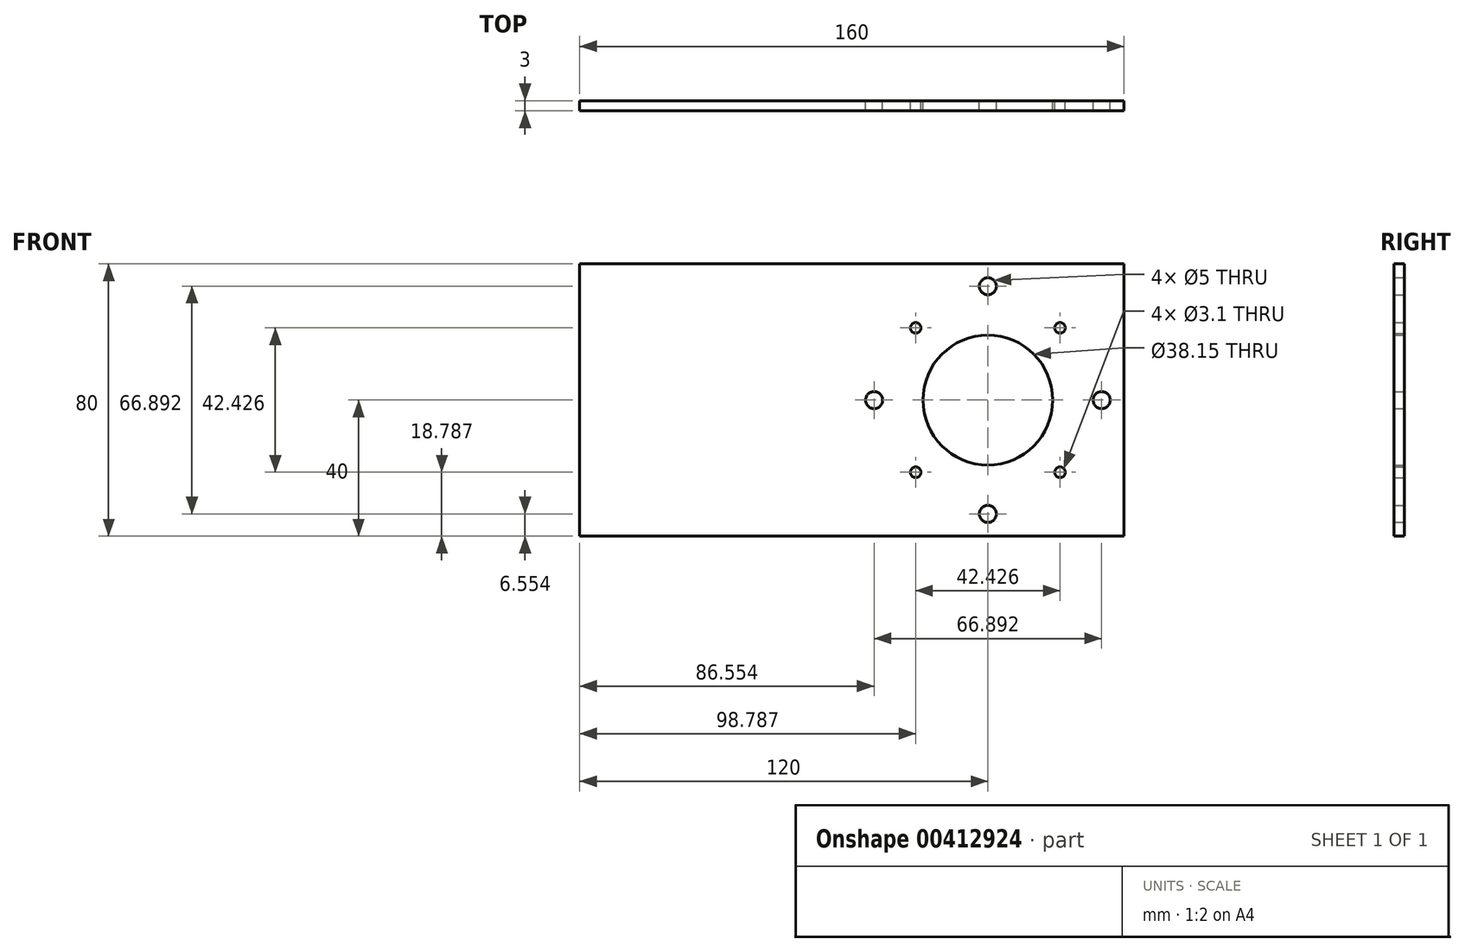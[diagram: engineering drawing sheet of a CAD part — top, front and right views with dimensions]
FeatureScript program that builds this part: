
annotation { "Feature Type Name" : "Feature", "Feature Type Description" : "" }
export const myFeature = defineFeature(function(context is Context, id is Id, definition is map)
    precondition{}
    {
        {
            var Q0;
            Q0=qCreatedBy(makeId("Front.planeOp"),FACE);
            var sketch = newSketch(context, id + "F0", { "sketchPlane" : qUnion([Q0])});
            skCircle(sketch, "E0", {"center": v(0, 0) * mm, "radius": 19.07 * mm});
            skCircle(sketch, "E1", {"center": v(-33.45, 0) * mm, "radius": 2.5 * mm});
            skCircle(sketch, "E2.1.0", {"center": v(0, -33.45) * mm, "radius": 2.5 * mm});
            skCircle(sketch, "E2.2.0", {"center": v(33.45, 0) * mm, "radius": 2.5 * mm});
            skCircle(sketch, "E2.3.0", {"center": v(0, 33.45) * mm, "radius": 2.5 * mm});
            skPoint(sketch, "E3.center", {"position": v(-0.05, 1.4) * mm});
            skLineSegment(sketch, "E4.bottom", {"start": v(-120, 40) * mm, "end": v(40, 40) * mm});
            skLineSegment(sketch, "E4.top", {"start": v(-120, -40) * mm, "end": v(40, -40) * mm});
            skLineSegment(sketch, "E4.left", {"start": v(-120, 40) * mm, "end": v(-120, -40) * mm});
            skLineSegment(sketch, "E4.right", {"start": v(40, 40) * mm, "end": v(40, -40) * mm});
            skCircle(sketch, "E5", {"center": v(-21.21, 21.21) * mm, "radius": 1.55 * mm});
            skCircle(sketch, "E6.1.0", {"center": v(-21.21, -21.21) * mm, "radius": 1.55 * mm});
            skCircle(sketch, "E6.2.0", {"center": v(21.21, -21.21) * mm, "radius": 1.55 * mm});
            skCircle(sketch, "E6.3.0", {"center": v(21.21, 21.21) * mm, "radius": 1.55 * mm});
            skSolve(sketch);
        }
        {
            var Q0;
            Q0=makeQuery(id+"F0.imprint","IMPRINT",FACE,{"disambiguationData":[TD([[makeQuery(id+"F0.imprint","IMPRINT",EDGE,{"derivedFrom":sQuery(id+"F0.wireOp",EDGE,"E0")}),-1.0]])]});
            extrude(context, id + "F1", {"entities" : qUnion([Q0]), "depth" : 3 * mm});
        }
    });
